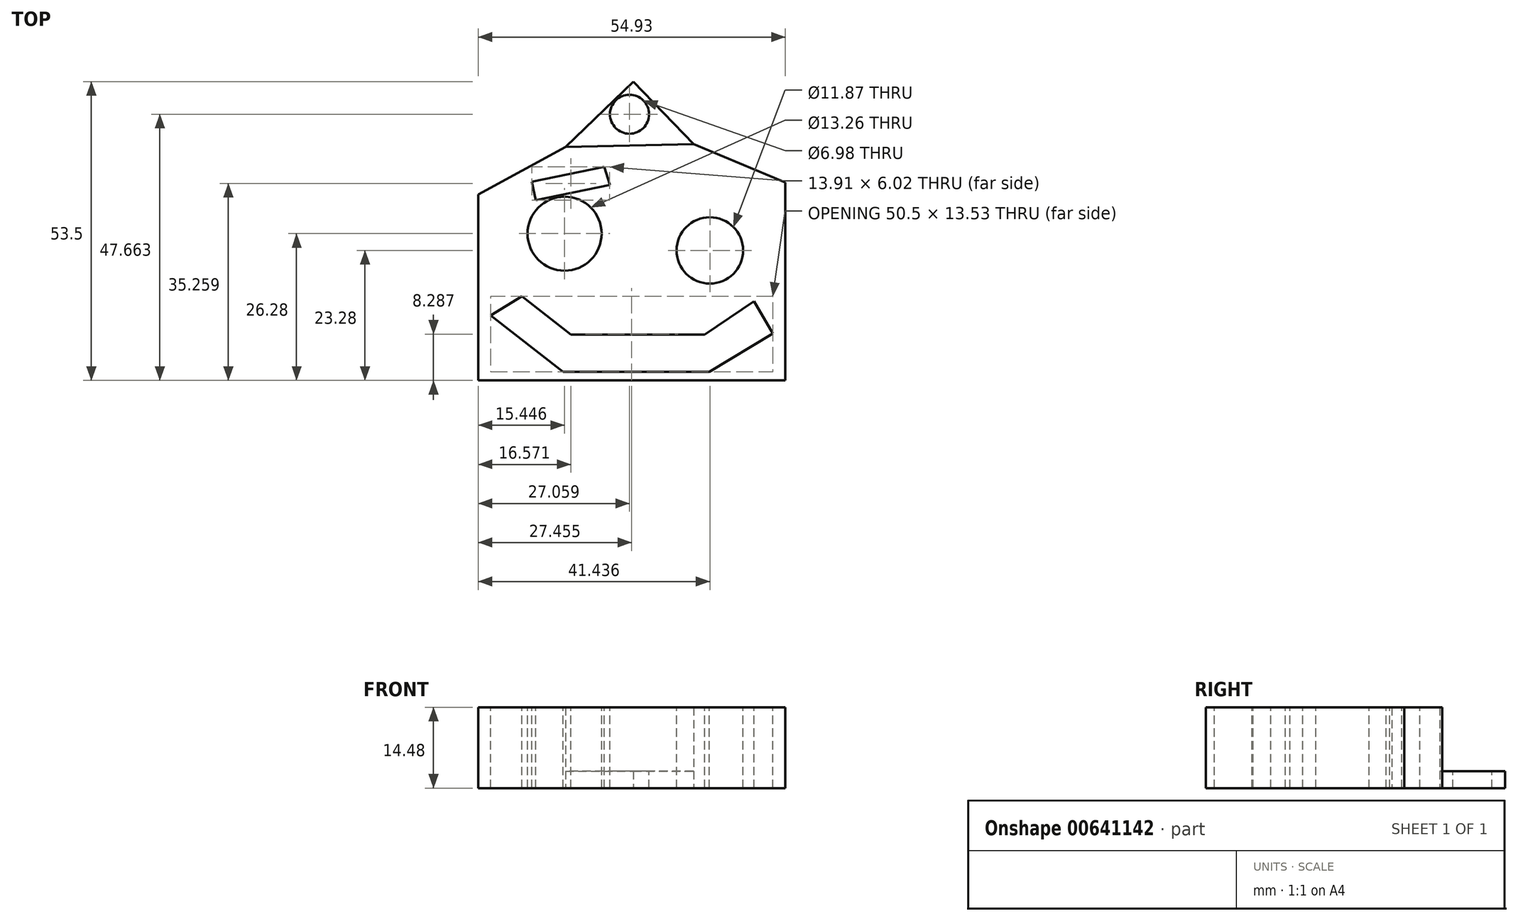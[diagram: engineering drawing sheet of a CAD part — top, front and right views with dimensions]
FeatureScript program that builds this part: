
annotation { "Feature Type Name" : "Feature", "Feature Type Description" : "" }
export const myFeature = defineFeature(function(context is Context, id is Id, definition is map)
    precondition{}
    {
        {
            var Q0;
            Q0=qCreatedBy(makeId("Top.planeOp"),FACE);
            var sketch = newSketch(context, id + "F0", { "sketchPlane" : qUnion([Q0])});
            skLineSegment(sketch, "E0", {"start": v(-12.12, 18.54) * mm, "end": v(0, 30.22) * mm});
            skLineSegment(sketch, "E1", {"start": v(0, 30.22) * mm, "end": v(10.8, 19.02) * mm});
            skLineSegment(sketch, "E2", {"start": v(10.8, 19.02) * mm, "end": v(-12.12, 18.54) * mm});
            skLineSegment(sketch, "E3", {"start": v(-12.12, 18.54) * mm, "end": v(-27.72, 10) * mm});
            skLineSegment(sketch, "E4", {"start": v(-27.72, 10) * mm, "end": v(-27.72, -23.28) * mm});
            skLineSegment(sketch, "E5", {"start": v(-27.72, -23.28) * mm, "end": v(27.2, -23.28) * mm});
            skLineSegment(sketch, "E6", {"start": v(27.2, -23.28) * mm, "end": v(27.2, 12.18) * mm});
            skLineSegment(sketch, "E7", {"start": v(27.2, 12.18) * mm, "end": v(10.8, 19.02) * mm});
            skSolve(sketch);
        }
        {
            var Q0;
            Q0=makeQuery(id+"F0.imprint","IMPRINT",FACE,{"disambiguationData":[TD([[makeQuery(id+"F0.imprint","IMPRINT",EDGE,{"derivedFrom":sQuery(id+"F0.wireOp",EDGE,"E2")}),1.0]])]});
            extrude(context, id + "F1", {"entities" : qUnion([Q0]), "depth" : 14.48 * mm, "offsetDistance" : 25.4 * mm});
        }
        {
            var Q0;
            Q0=makeQuery(id+"F1.opExtrude","CAP_FACE",FACE,{"disambiguationData":[OSD([sQuery(id+"F0.wireOp",EDGE,"E2"),sQuery(id+"F0.wireOp",EDGE,"E3"),sQuery(id+"F0.wireOp",EDGE,"E4"),sQuery(id+"F0.wireOp",EDGE,"E5"),sQuery(id+"F0.wireOp",EDGE,"E6"),sQuery(id+"F0.wireOp",EDGE,"E7")])],"isStart":false});
            var sketch = newSketch(context, id + "F2", { "sketchPlane" : qUnion([Q0])});
            skCircle(sketch, "E8", {"center": v(-12.27, 3) * mm, "radius": 6.63 * mm});
            skCircle(sketch, "E9", {"center": v(13.72, 0) * mm, "radius": 5.94 * mm});
            skSolve(sketch);
        }
        {
            var Q0;
            Q0=makeQuery(id+"F2.imprint","IMPRINT",FACE,{"disambiguationData":[TD([[makeQuery(id+"F2.imprint","IMPRINT",EDGE,{"derivedFrom":sQuery(id+"F2.wireOp",EDGE,"E8")}),-1.0]])]});
            var sketch = newSketch(context, id + "F3", { "sketchPlane" : qUnion([Q0])});
            skLineSegment(sketch, "E10", {"start": v(-19.91, -8.23) * mm, "end": v(-11.14, -15.07) * mm});
            skLineSegment(sketch, "E11", {"start": v(-11.14, -15.07) * mm, "end": v(12.8, -15.07) * mm});
            skLineSegment(sketch, "E12", {"start": v(12.8, -15.07) * mm, "end": v(21.6, -9.08) * mm});
            skLineSegment(sketch, "E13", {"start": v(21.6, -9.08) * mm, "end": v(12.8, -15.07) * mm});
            skLineSegment(sketch, "E14", {"start": v(-18.1, 12.27) * mm, "end": v(-5.17, 14.99) * mm});
            skLineSegment(sketch, "E15", {"start": v(21.07, 11.02) * mm, "end": v(10.32, 14.99) * mm});
            skLineSegment(sketch, "E16", {"start": v(10.32, 14.99) * mm, "end": v(21.07, 11.02) * mm});
            skLineSegment(sketch, "E17", {"start": v(-18.1, 12.27) * mm, "end": v(-17.41, 8.97) * mm});
            skLineSegment(sketch, "E18", {"start": v(-17.41, 8.97) * mm, "end": v(-4.2, 11.75) * mm});
            skLineSegment(sketch, "E19", {"start": v(-4.2, 11.75) * mm, "end": v(-5.17, 14.99) * mm});
            skLineSegment(sketch, "E20", {"start": v(10.32, 14.99) * mm, "end": v(9.32, 12.27) * mm});
            skLineSegment(sketch, "E21", {"start": v(9.32, 12.27) * mm, "end": v(20.9, 8) * mm});
            skLineSegment(sketch, "E22", {"start": v(20.9, 8) * mm, "end": v(21.07, 11.02) * mm});
            skLineSegment(sketch, "E23", {"start": v(-19.91, -8.23) * mm, "end": v(-25.52, -11.65) * mm});
            skPoint(sketch, "E23.endSnap0", {"position": v(-15.53, -11.65) * mm});
            skLineSegment(sketch, "E24", {"start": v(-25.52, -11.65) * mm, "end": v(-12.56, -21.76) * mm});
            skLineSegment(sketch, "E25", {"start": v(-12.56, -21.76) * mm, "end": v(13.6, -21.76) * mm});
            skLineSegment(sketch, "E26", {"start": v(13.6, -21.76) * mm, "end": v(24.99, -14.88) * mm});
            skLineSegment(sketch, "E27", {"start": v(24.99, -14.88) * mm, "end": v(21.6, -9.08) * mm});
            skSolve(sketch);
        }
        {
            var Q0;
            Q0=makeQuery(id+"F2.imprint","IMPRINT",FACE,{"disambiguationData":[TD([[makeQuery(id+"F2.imprint","IMPRINT",EDGE,{"derivedFrom":sQuery(id+"F2.wireOp",EDGE,"E8")}),1.0]])]});
            var Q1;
            Q1=makeQuery(id+"F2.imprint","IMPRINT",FACE,{"disambiguationData":[TD([[makeQuery(id+"F2.imprint","IMPRINT",EDGE,{"derivedFrom":sQuery(id+"F2.wireOp",EDGE,"E9")}),1.0]])]});
            extrude(context, id + "F4", {"entities" : qUnion([Q0, Q1]), "operationType" : NewBodyOperationType.REMOVE, "oppositeDirection" : true, "depth" : 25.4 * mm, "offsetDistance" : 25.4 * mm});
        }
        {
            var Q0;
            Q0=makeQuery(id+"F3.imprint","IMPRINT",FACE,{"disambiguationData":[TD([[makeQuery(id+"F3.imprint","IMPRINT",EDGE,{"derivedFrom":sQuery(id+"F3.wireOp",EDGE,"E10")}),-1.0]])]});
            var Q1;
            Q1=makeQuery(id+"F3.imprint","IMPRINT",FACE,{"disambiguationData":[TD([[makeQuery(id+"F3.imprint","IMPRINT",EDGE,{"derivedFrom":sQuery(id+"F3.wireOp",EDGE,"E16")}),-1.0]])]});
            var Q2;
            Q2=makeQuery(id+"F3.imprint","IMPRINT",FACE,{"disambiguationData":[TD([[makeQuery(id+"F3.imprint","IMPRINT",EDGE,{"derivedFrom":sQuery(id+"F3.wireOp",EDGE,"E14")}),-1.0]])]});
            extrude(context, id + "F5", {"entities" : qUnion([Q0, Q1, Q2]), "operationType" : NewBodyOperationType.REMOVE, "oppositeDirection" : true, "depth" : 25.4 * mm, "offsetDistance" : 25.4 * mm});
        }
        {
            var Q0;
            Q0=makeQuery(id+"F0.imprint","IMPRINT",FACE,{"disambiguationData":[TD([[makeQuery(id+"F0.imprint","IMPRINT",EDGE,{"derivedFrom":sQuery(id+"F0.wireOp",EDGE,"E0")}),-1.0]])]});
            extrude(context, id + "F6", {"entities" : qUnion([Q0]), "operationType" : NewBodyOperationType.ADD, "depth" : 3.05 * mm, "offsetDistance" : 25.4 * mm});
        }
        {
            var Q0;
            Q0=makeQuery(id+"F6.opExtrude","CAP_FACE",FACE,{"disambiguationData":[OSD([sQuery(id+"F0.wireOp",EDGE,"E0"),sQuery(id+"F0.wireOp",EDGE,"E1"),sQuery(id+"F0.wireOp",EDGE,"E2")])],"isStart":false});
            var sketch = newSketch(context, id + "F7", { "sketchPlane" : qUnion([Q0])});
            skCircle(sketch, "E28", {"center": v(-0.66, 24.38) * mm, "radius": 3.5 * mm});
            skPoint(sketch, "E28.centerSnap0", {"position": v(-0.66, 18.78) * mm});
            skPoint(sketch, "E28.centerSnap1", {"position": v(-6.06, 24.38) * mm});
            skSolve(sketch);
        }
        {
            var Q0;
            Q0 = qSketchRegion(id + "F7", true);
            extrude(context, id + "F8", {"entities" : qUnion([Q0]), "operationType" : NewBodyOperationType.REMOVE, "oppositeDirection" : true, "depth" : 25.4 * mm, "offsetDistance" : 25.4 * mm});
        }
    });
